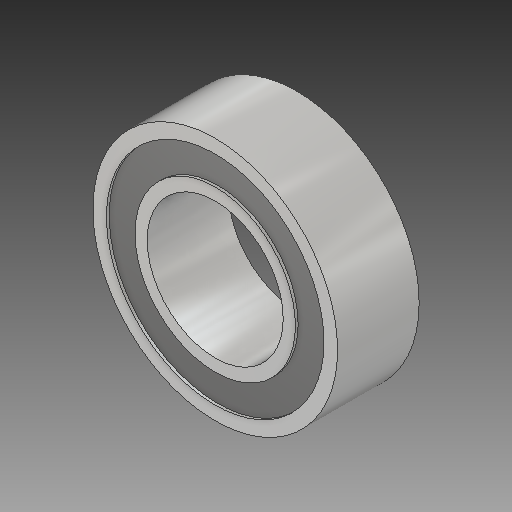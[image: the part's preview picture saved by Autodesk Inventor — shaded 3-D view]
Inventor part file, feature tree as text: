
AUTODESK INVENTOR PART (.ipt)
format: ipt  version: 2018 (Build 220112000, 112)  size: 158,720 bytes
history: native  units: in
note: dims shown in document units (in); Inventor stores cm internally (conversion verified against a paired STEP export)
features: extrude x3, sketch x3, projected_geometry x1
ambient origin geometry x8: Origin, YZ Plane, XZ Plane, XY Plane, X Axis, Y Axis, Z Axis, Center Point
bodies: Solid1 (feature_tree)
feature tree (7):
  extrude  "Extrusion1"  Depth=0.1969in
  extrude  "Extrusion2"  Depth=0.1181in
  extrude  "Extrusion3"  Depth=0.0039in TaperAngle=0.0deg
  sketch  "Sketch1"  dims[d0=0.3543in d1=0.1969in]
  sketch  "Sketch2"  dims[d2=0.1181in d3=0.0in d4=0.2323in]
  projected_geometry  "Projected Loop1"
  sketch  "Sketch3"  dims[d5=0.0197in d6=0.0039in d7=0.0in d8=0.0039in d9=0.0in]
